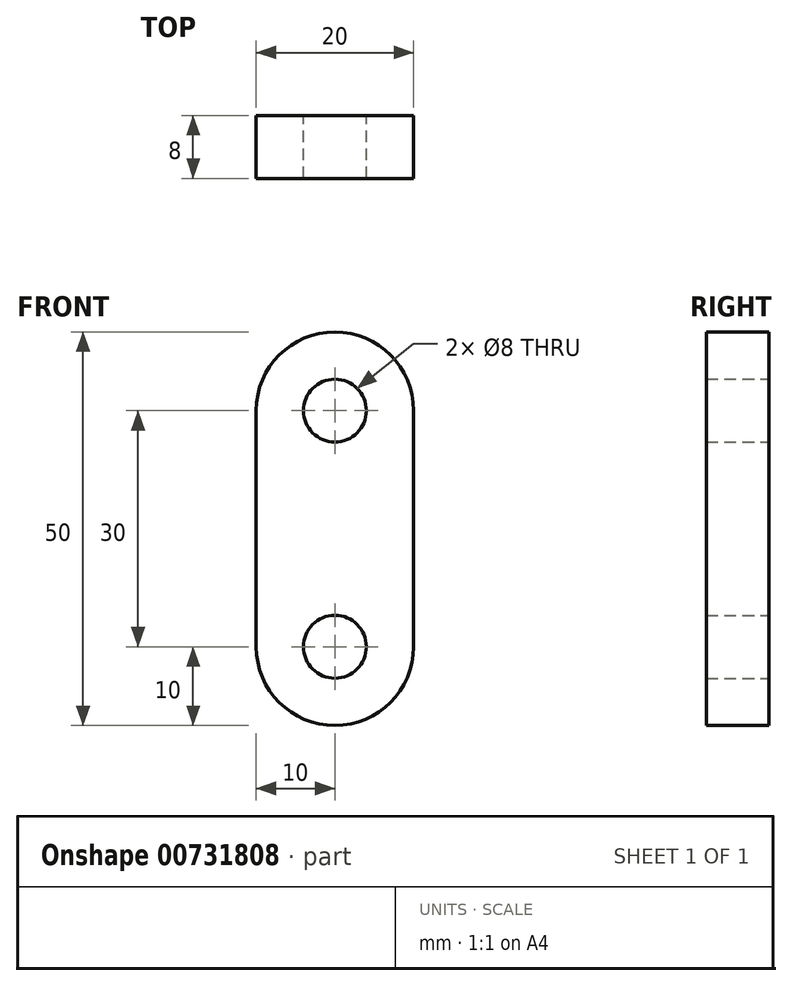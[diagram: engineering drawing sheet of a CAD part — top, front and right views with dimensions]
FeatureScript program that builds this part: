
annotation { "Feature Type Name" : "Feature", "Feature Type Description" : "" }
export const myFeature = defineFeature(function(context is Context, id is Id, definition is map)
    precondition{}
    {
        {
            var Q0;
            Q0=qCreatedBy(makeId("Front.planeOp"),FACE);
            var sketch = newSketch(context, id + "F0", { "sketchPlane" : qUnion([Q0])});
            skCircle(sketch, "E0", {"center": v(0, 0) * mm, "radius": 4 * mm});
            skArc(sketch, "E1", {"start": v(-10, 0) * mm, "mid": v(0, -10) * mm, "end": v(10, 0) * mm});
            skLineSegment(sketch, "E2", {"start": v(-10, 0) * mm, "end": v(-10, 30) * mm});
            skLineSegment(sketch, "E3", {"start": v(10, 0) * mm, "end": v(10, 30) * mm});
            skArc(sketch, "E4", {"start": v(10, 30) * mm, "mid": v(0, 40) * mm, "end": v(-10, 30) * mm});
            skCircle(sketch, "E5", {"center": v(0, 30) * mm, "radius": 4 * mm});
            skSolve(sketch);
        }
        {
            var Q0;
            Q0 = qSketchRegion(id + "F0", true);
            extrude(context, id + "F1", {"entities" : qUnion([Q0]), "depth" : 8 * mm, "offsetDistance" : 25 * mm});
        }
    });
